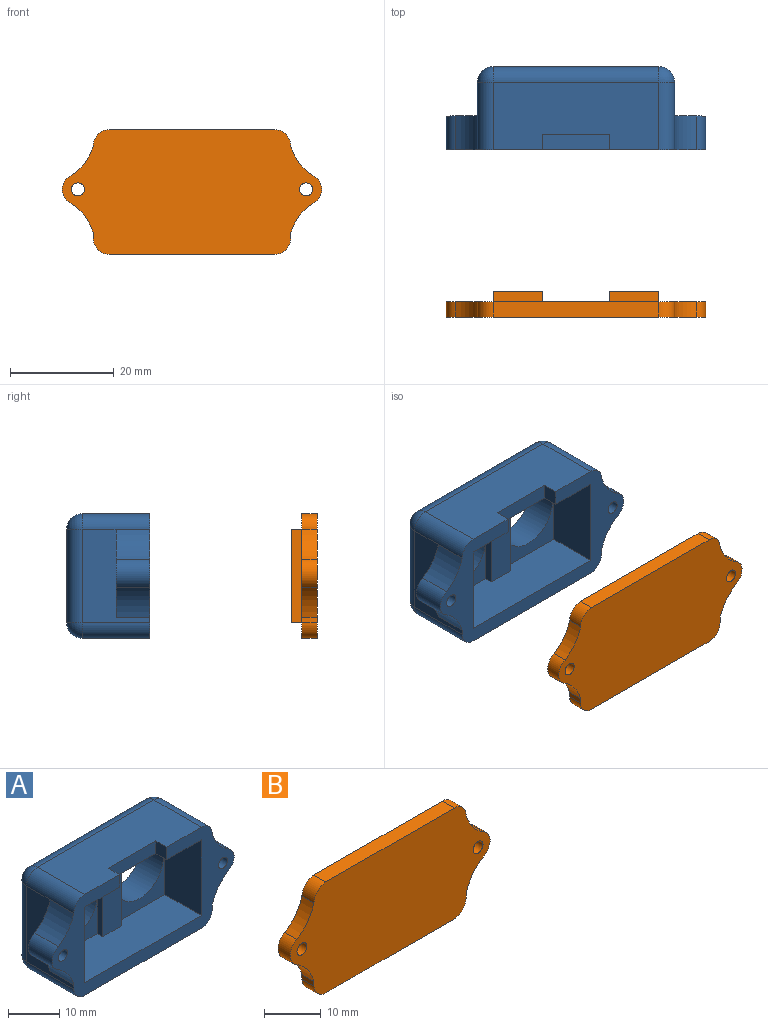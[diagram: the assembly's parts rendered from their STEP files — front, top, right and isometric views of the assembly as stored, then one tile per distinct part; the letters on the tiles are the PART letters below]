
ASSEMBLY  parts=2 mates=1
PART A: 42 faces, bbox 50x16x24 mm
  f0: plane 50x24mm, normal (0,-1,0), area 375.8mm2, adj f1,f4,f7,f8,f9,f10,f11,f12
  f1: plane 32x13mm, normal (0,0,1), area 377mm2, adj f0,f7,f12,f31,f32,f33,f34
  f2: plane 18x1.5mm, normal (-1,0,0), area 27mm2, adj f15,f17,f18,f30
  f3: plane 18x1.5mm, normal (1,0,0), area 27mm2, adj f16,f17,f18,f30
  f4: plane 18x13mm, normal (1,0,0), area 123.5mm2, adj f0,f11,f12,f25,f29,f38
  f5: cylinder r=6.5mm len=13mm, axis (0,1,0), area 245mm2, adj f13,f15
  f6: cylinder r=6.5mm len=13mm, axis (0,1,0), area 245mm2, adj f13,f16
  f7: cylinder r=3mm len=13mm, axis (0,1,0), area 61.3mm2, adj f0,f1,f8,f21,f35
  f8: plane 18x13mm, normal (-1,0,0), area 123.5mm2, adj f0,f7,f9,f20,f24,f37
  f9: cylinder r=3mm len=13mm, axis (0,1,0), area 61.3mm2, adj f0,f8,f10,f39
  f10: plane 32x13mm, normal (0,0,-1), area 416mm2, adj f0,f9,f11,f41
  f11: cylinder r=3mm len=13mm, axis (0,1,0), area 61.3mm2, adj f0,f4,f10,f40
  f12: cylinder r=3mm len=13mm, axis (0,1,0), area 61.3mm2, adj f0,f1,f4,f27,f36
  f13: plane 32x18mm, normal (0,1,0), area 310.5mm2, adj f5,f6,f34,f37,f38,f41
  f14: plane 18x10mm, normal (1,0,0), area 180mm2, adj f0,f15,f17,f18
  f15: plane 18x13.4mm, normal (0,-1,0), area 108.5mm2, adj f2,f5,f14,f17,f18
  f16: plane 18x13.4mm, normal (0,-1,0), area 108.5mm2, adj f3,f6,f17,f18,f19
  f17: plane 32x10mm, normal (0,0,-1), area 273.2mm2, adj f0,f2,f3,f14,f15,f16,f19,f30
  f18: plane 32x10mm, normal (0,0,1), area 312.2mm2, adj f0,f2,f3,f14,f15,f16,f19,f30
  f19: plane 18x10mm, normal (-1,0,0), area 180mm2, adj f0,f16,f17,f18
  f20: cylinder r=10mm len=6.5mm, axis (0,-1,0), area 47.6mm2, adj f0,f8,f22,f24
  f21: cylinder r=10mm len=6.5mm, axis (0,-1,0), area 47.6mm2, adj f0,f7,f22,f24
  f22: cylinder r=3mm len=6.5mm, axis (0,-1,0), area 44.6mm2, adj f0,f20,f21,f24
  f23: cylinder r=1.25mm len=6.5mm, axis (0,-1,0), area 51.1mm2, adj f0,f24
  f24: plane 17x6mm, normal (0,1,0), area 43.3mm2, adj f8,f20,f21,f22,f23
  f25: cylinder r=10mm len=6.5mm, axis (0,-1,0), area 47.6mm2, adj f0,f4,f26,f29
  f26: cylinder r=3mm len=6.5mm, axis (0,-1,0), area 44.6mm2, adj f0,f25,f27,f29
  f27: cylinder r=10mm len=6.5mm, axis (0,-1,0), area 47.6mm2, adj f0,f12,f26,f29
  f28: cylinder r=1.25mm len=6.5mm, axis (0,-1,0), area 51.1mm2, adj f0,f29
  f29: plane 17x6mm, normal (0,1,0), area 43.3mm2, adj f4,f25,f26,f27,f28
  f30: plane 18x5.2mm, normal (0,-1,0), area 93.6mm2, adj f2,f3,f17,f18
  f31: plane 3x3mm, normal (-1,0,0), area 9mm2, adj f0,f1,f17,f33
  f32: plane 3x3mm, normal (1,0,0), area 9mm2, adj f0,f1,f17,f33
  f33: plane 13x3mm, normal (0,-1,0), area 39mm2, adj f1,f17,f31,f32
  f34: cylinder r=3mm len=32mm, axis (-1,0,0), area 150.8mm2, adj f1,f13,f35,f36
  f35: sphere r=3mm, area 14.1mm2, adj f7,f34,f37
  f36: sphere r=3mm, area 14.1mm2, adj f12,f34,f38
  f37: cylinder r=3mm len=18mm, axis (0,0,-1), area 84.8mm2, adj f8,f13,f35,f39
  f38: cylinder r=3mm len=18mm, axis (0,0,1), area 84.8mm2, adj f4,f13,f36,f40
  f39: sphere r=3mm, area 14.1mm2, adj f9,f37,f41
  f40: sphere r=3mm, area 14.1mm2, adj f11,f38,f41
  f41: cylinder r=3mm len=32mm, axis (1,0,0), area 150.8mm2, adj f10,f13,f39,f40
PART B: 28 faces, bbox 50x5x24 mm
  f0: plane 50x24mm, normal (0,1,0), area 648.8mm2, adj f1,f2,f3,f4,f5,f6,f7,f8
  f1: plane 32x3mm, normal (0,0,1), area 96mm2, adj f0,f2,f16,f17
  f2: cylinder r=3mm len=3mm, axis (0,1,0), area 14.1mm2, adj f0,f1,f3,f17
  f3: cylinder r=10mm len=5.77mm, axis (0,1,0), area 22mm2, adj f0,f2,f4,f17
  f4: cylinder r=3mm len=5.46mm, axis (0,1,0), area 20.6mm2, adj f0,f3,f5,f17
  f5: cylinder r=10mm len=5.77mm, axis (0,1,0), area 22mm2, adj f0,f4,f6,f17
  f6: plane 3x1mm, normal (-1,0,0), area 3mm2, adj f0,f5,f7,f17
  f7: cylinder r=3mm len=3mm, axis (0,1,0), area 14.1mm2, adj f0,f6,f8,f17
  f8: plane 32x3mm, normal (0,0,-1), area 96mm2, adj f0,f7,f9,f17
  f9: cylinder r=3mm len=3mm, axis (0,1,0), area 14.1mm2, adj f0,f8,f10,f17
  f10: plane 3x1mm, normal (1,0,0), area 3mm2, adj f0,f9,f11,f17
  f11: cylinder r=10mm len=5.77mm, axis (0,1,0), area 22mm2, adj f0,f10,f12,f17
  f12: cylinder r=3mm len=5.46mm, axis (0,1,0), area 20.6mm2, adj f0,f11,f13,f17
  f13: cylinder r=10mm len=5.77mm, axis (0,1,0), area 22mm2, adj f0,f12,f16,f17
  f14: cylinder r=1.25mm len=3mm, axis (0,1,0), area 23.6mm2, adj f0,f17
  f15: cylinder r=1.25mm len=3mm, axis (0,1,0), area 23.6mm2, adj f0,f17
  f16: cylinder r=3mm len=3mm, axis (0,1,0), area 14.1mm2, adj f0,f1,f13,f17
  f17: plane 50x24mm, normal (0,-1,0), area 990.8mm2, adj f1,f2,f3,f4,f5,f6,f7,f8
  f18: plane 9.5x2mm, normal (0,0,1), area 19mm2, adj f0,f19,f21,f22
  f19: plane 18x2mm, normal (-1,0,0), area 36mm2, adj f0,f18,f20,f22
  f20: plane 9.5x2mm, normal (0,0,-1), area 19mm2, adj f0,f19,f21,f22
  f21: plane 18x2mm, normal (1,0,0), area 36mm2, adj f0,f18,f20,f22
  f22: plane 18x9.5mm, normal (0,1,0), area 171mm2, adj f18,f19,f20,f21
  f23: plane 18x2mm, normal (-1,0,0), area 36mm2, adj f0,f24,f26,f27
  f24: plane 9.5x2mm, normal (0,0,-1), area 19mm2, adj f0,f23,f25,f27
  f25: plane 18x2mm, normal (1,0,0), area 36mm2, adj f0,f24,f26,f27
  f26: plane 9.5x2mm, normal (0,0,1), area 19mm2, adj f0,f23,f25,f27
  f27: plane 18x9.5mm, normal (0,1,0), area 171mm2, adj f23,f24,f25,f26
PLACE A t=(-1.04,35.97,12.33)mm fixed
PLACE B t=(-1.04,20.68,12.33)mm
MATE slider B.f0 <-> A.f0  axis (0,1,0) through (14.96,-9.32,23.83)mm
